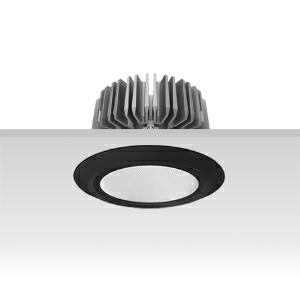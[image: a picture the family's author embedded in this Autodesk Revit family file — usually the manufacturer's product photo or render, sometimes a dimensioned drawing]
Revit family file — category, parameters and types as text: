
# Revit family: 3f_filippi_-_3f_reno_bianco_ampio_3f_filippi_-_30349_a01036_-_3f_reno_150_wh_3000-840_wide___vs_bk_59ec
name_source: partatom
category: Lighting Fixtures
units: mm (PartAtom-declared; Revit-internal decimal feet)

## family parameters
Cut with Voids When Loaded = No
Host = Face
Light Source = No
Part Type = Normal
Room Calculation Point = No
Round Connector Dimension = Use Diameter
Shared = No

## types (1)
- 3F Filippi - 3F Reno Bianco Ampio (1 x LED, 2293 lm, 28 W, 4000 K)
    Apparent Load = 28 VA
    Approval mark = CE
    CIE Flux Codes = 74 93 99 100 100
    Color Rendering = 80
    Color Temperature = 4000 K
    Control Gear = Electronic ballast
    Default Elevation = 1800 mm
    Description = ILLUMINOTECHNICAL
Luminous efficiency 100% (DLOR 100%, ULOR 0%).
Initial luminous flux of the luminaire 2293 lm.
Direct symmetric wide distribution.
Installation Interdistance Transv.D = 1.12 x hu - Long.D = 1.11 x hu.
Tabular UGR (CIE 117 - 4H-8H; S=0.25H; 70/50/20): RUG 23.9 - 23.7.
Beam angle: 74° - 73°.
Luminous efficacy 82 lm/W.
Lifetime (L90/B10): 30000 h. (tq+25°C)
Lifetime (L85/B10): 50000 h. (tq+25°C)
Lifetime (L70/B10): 80000 h. (tq+25°C)
Sudden decreased luminous flux after 50000 hours: 0% (C0).
Photobiological safety in compliance with IEC/TR 62778: RG0 risk exempt, (IEC 62471).
In compliance with IEC/EN 62722-2-1 - IEC/EN 62717 standards.

SOURCE
Compact LED module 3000/840.
Energy efficiency class (UE 2019/2020 - UE 2019/2015): D.
CIE 13.3 Colour rendering index: CRI >80 (R9 <50%).
IES TM-30 Fidelity Index: Rf = 84 Rg = 95.
CCT nominal colour temperature 4000 K.
Colour initial tolerance (MacAdam): SDCM 3.
Zhaga Book 3 compliant.

MECHANICAL
Passive heat dissipator in die-casting aluminium, oversized, for optimum thermal management of the LED module.
Parabolic element with graduated/concentric rings in white polycarbonate.
Transparent external lens with glossy and satin differentiated surfaces, with a cooling and anti-insect system in methacrylate (PMMA).
Fastening spring clips in stainless steel.
Dimensions: diameter 176 mm, height 111 mm. Weight 1.45 kg.
IP44 protection degree for exposed part, IP20 for recessed part.
Mechanical strength to impacts IK06 (1 joule).
Glow-wire test resistance 650°C.

ELECTRICAL
Wiring on a separate unit.
Halogen Free electronic wiring 230V-50/60Hz, power factor 0.95, THD <25%, constant output current, SELV, class II, 1 driver.
Power of the luminaire 28 W.
ENEC - CE.
SAFE FLICKER: PstLM=<1 and SVM=<0.4 (IEC TR 61547-1 and IEC TR 63158), to ensure a more comfortable and safe light.
Luminaire compliant with EN 60598-2-22 for power supply from a centralised emergency system CPSS (Central Power Supply System), not incorporated in the luminaire - high risk areas excluded. The default power and flux are 100% in AC and 100% in DC.
Ambient temperature from 0°C to +25°C.
Temperature class T6 max 85°C.
Relative humidity UR: <85%.

INSTALLATION
Pull-up recessed fitting.
False ceiling carving: 150 mm.
All accessories dedicated to this product are available on the Catalog and on our website www.3F-Filippi.com.

ACCESSORIES
A01036 - Anti-glare microprismatic VS moulded glass, tempered, not flammable, locked and in line with the trim, in black polycarbonate.

APPLICATIONS
Environments: architectural, commercial, exhibition areas, transit areas, corridors, shops, display windows, service areas.
In false ceilings with narrow voids.

WARNING
Luminaire designed for disposal/recycling at end-of-life.
Replaceable (LED only) light source by a professional. Replaceable control gear by a professional.
    Height = 0 mm  [stored 0 ft]
    Lamp = 1 x LED
    Lamp Light Flux = 2293 lm
    Lamp Power = 28 W
    Lamp count = 1
    Length = 176 mm
    Lifetime = 50000 h
    Luminous efficacy = 82 lm/W
    Manufacturer = 3F Filippi
    ModVariant = No
    Model = 3F Filippi - 30349+A01036 - 3F Reno 150 WH 3000-840 WIDE + VS BK
    Mounting Place = Ceiling
    Mounting Type = Recessed
    Number of Poles = 1
    OnlyDefault = Yes
    Power Factor = 1
    Product Name = 3F Filippi - 3F Reno Bianco Ampio
    Product group = recessed luminaire
    ProductGroupID = 4
    Protection Class = Protection class II
    Protection Degree = IP 20
    RLX_Detail_Level = 1
    RLX_Emergency_Light_Flux = 0 lm
    RLX_Emergency_Type = 0
    RLX_Emergency_Type_DB = No
    RlxData = <blob elided: 85621 chars, md5=8bc4f6ed>
    Socket = socket
    Standby Power = 0 W
    System Light Flux = 2293 lm
    System Power = 28 W
    Type Comments = Product without accessories
    Type Image = 3ffilippi_3f_reno_150_bk_vs_smp.jpg
    URL = http://relux.com
    VarID = ---
    Voltage = 0 V
    Weight = 0.00 kg
    Width = 0 mm  [stored 0 ft]

note: [stored X ft] marks values corroborated as IEEE doubles in the binary element streams (Revit-internal decimal feet)

## geometry (parser evidence)
native form markers: Blend x4, Sweep x9
no freeform markers — native parametric forms only
